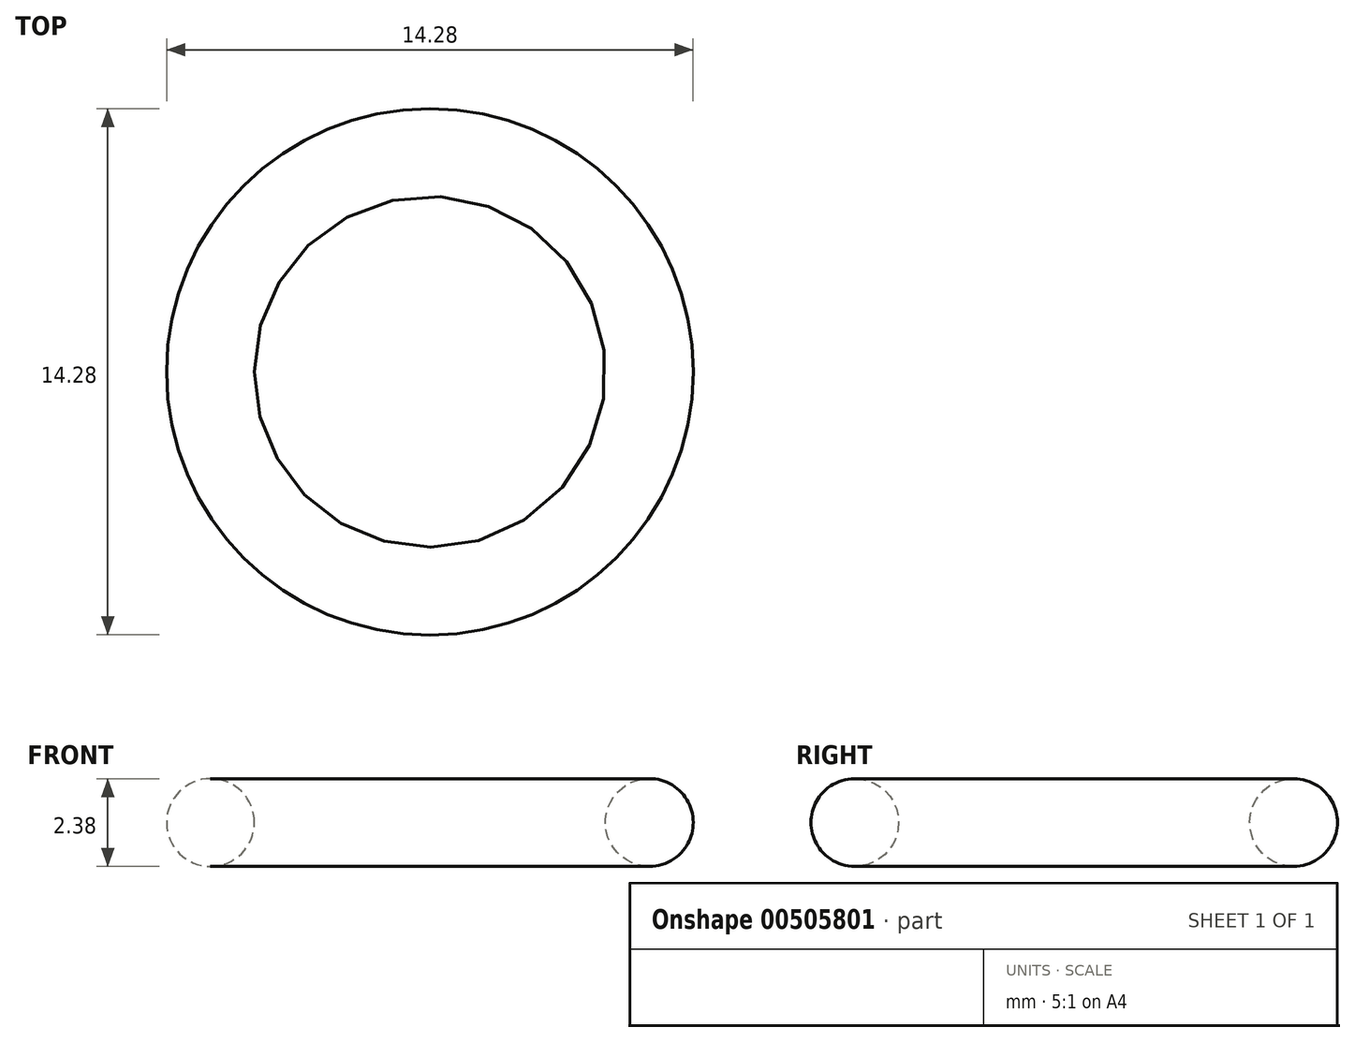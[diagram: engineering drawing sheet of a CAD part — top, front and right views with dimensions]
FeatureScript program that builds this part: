
annotation { "Feature Type Name" : "Feature", "Feature Type Description" : "" }
export const myFeature = defineFeature(function(context is Context, id is Id, definition is map)
    precondition{}
    {
        {
            var Q0;
            Q0=qCreatedBy(makeId("Front.planeOp"),FACE);
            var sketch = newSketch(context, id + "F0", { "sketchPlane" : qUnion([Q0])});
            skCircle(sketch, "E0", {"center": v(-5.95, 0) * mm, "radius": 1.2 * mm});
            skLineSegment(sketch, "E1", {"start": v(0, 0) * mm, "end": v(0, 25.4) * mm, "construction": true});
            skPoint(sketch, "E2", {"position": v(-4.76, 0) * mm});
            skPoint(sketch, "E3", {"position": v(-7.14, 0) * mm});
            skSolve(sketch);
        }
        {
            var Q0;
            Q0=makeQuery(id+"F0.imprint","IMPRINT",FACE,{"disambiguationData":[TD([[makeQuery(id+"F0.imprint","IMPRINT",EDGE,{"derivedFrom":sQuery(id+"F0.wireOp",EDGE,"E0")}),1.0]])]});
            var Q1;
            Q1=sQuery(id+"F0.wireOp",EDGE,"E1");
            revolve(context, id + "F1", {"entities" : qUnion([Q0]), "axis" : qUnion([Q1]), "revolveType" : RevolveType.FULL});
        }
    });
